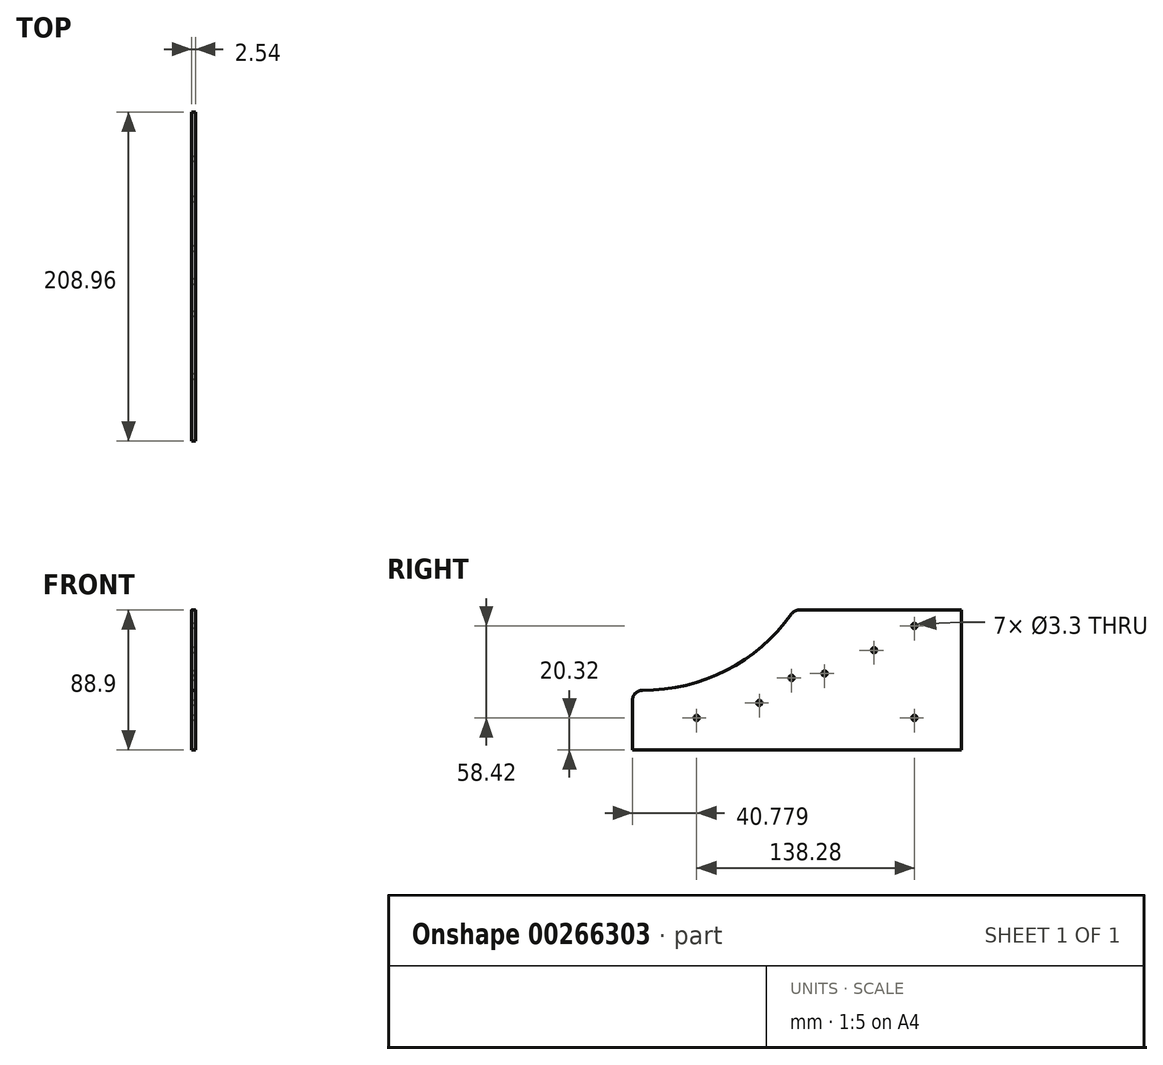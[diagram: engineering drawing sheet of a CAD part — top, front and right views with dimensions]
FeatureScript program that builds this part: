
annotation { "Feature Type Name" : "Feature", "Feature Type Description" : "" }
export const myFeature = defineFeature(function(context is Context, id is Id, definition is map)
    precondition{}
    {
        {
            var Q0;
            Q0=qCreatedBy(makeId("Right.planeOp"),FACE);
            var sketch = newSketch(context, id + "F0", { "sketchPlane" : qUnion([Q0])});
            skLineSegment(sketch, "E0", {"start": v(-102.71, 0) * mm, "end": v(106.25, 0) * mm});
            skLineSegment(sketch, "E1", {"start": v(106.25, 0) * mm, "end": v(106.25, 88.9) * mm});
            skLineSegment(sketch, "E2", {"start": v(-102.71, 31.45) * mm, "end": v(-102.71, 0) * mm});
            skLineSegment(sketch, "E3", {"start": v(3.34, 88.9) * mm, "end": v(106.25, 88.9) * mm});
            skCircle(sketch, "E4", {"center": v(76.35, 78.74) * mm, "radius": 1.65 * mm});
            skCircle(sketch, "E5", {"center": v(50.76, 63.33) * mm, "radius": 1.65 * mm});
            skCircle(sketch, "E6", {"center": v(-1.63, 45.72) * mm, "radius": 1.65 * mm});
            skCircle(sketch, "E7", {"center": v(19.3, 48.53) * mm, "radius": 1.65 * mm});
            skCircle(sketch, "E8", {"center": v(-22.15, 29.87) * mm, "radius": 1.65 * mm});
            skCircle(sketch, "E9", {"center": v(-61.93, 20.32) * mm, "radius": 1.65 * mm});
            skCircle(sketch, "E10", {"center": v(76.35, 20.32) * mm, "radius": 1.65 * mm});
            skArc(sketch, "E11", {"start": v(-96.32, 37.8) * mm, "mid": v(-43.16, 50.46) * mm, "end": v(-1.84, 86.23) * mm});
            skPoint(sketch, "E12.orphan", {"position": v(-102.71, 88.9) * mm});
            skPoint(sketch, "E13.visualSharp", {"position": v(-102.71, 38.02) * mm});
            skArc(sketch, "E13.filletArc", {"start": v(-96.32, 37.8) * mm, "mid": v(-100.84, 35.96) * mm, "end": v(-102.71, 31.45) * mm});
            skPoint(sketch, "E14.visualSharp", {"position": v(0, 88.9) * mm});
            skArc(sketch, "E14.filletArc", {"start": v(3.34, 88.9) * mm, "mid": v(0.42, 88.2) * mm, "end": v(-1.84, 86.23) * mm});
            skSolve(sketch);
        }
        {
            var Q0;
            Q0=makeQuery(id+"F0.imprint","IMPRINT",FACE,{"disambiguationData":[TD([[makeQuery(id+"F0.imprint","IMPRINT",EDGE,{"derivedFrom":sQuery(id+"F0.wireOp",EDGE,"E0")}),1.0]])]});
            extrude(context, id + "F1", {"entities" : qUnion([Q0]), "depth" : 2.54 * mm});
        }
    });
